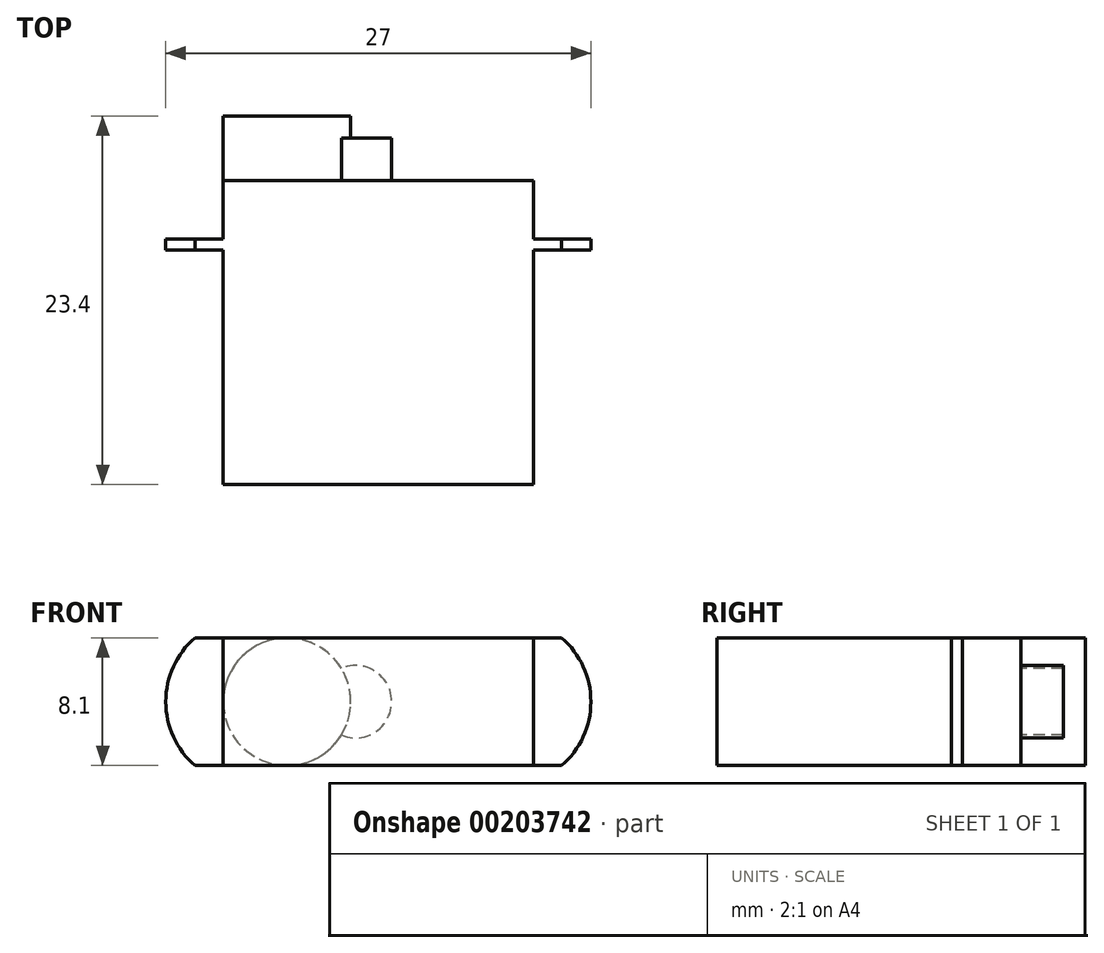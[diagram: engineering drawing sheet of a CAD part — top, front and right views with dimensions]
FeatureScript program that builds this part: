
annotation { "Feature Type Name" : "Feature", "Feature Type Description" : "" }
export const myFeature = defineFeature(function(context is Context, id is Id, definition is map)
    precondition{}
    {
        {
            var Q0;
            Q0=qCreatedBy(makeId("Top.planeOp"),FACE);
            var sketch = newSketch(context, id + "F0", { "sketchPlane" : qUnion([Q0])});
            skLineSegment(sketch, "E0.bottom", {"start": v(9.85, -9.65) * mm, "end": v(-9.85, -9.65) * mm});
            skLineSegment(sketch, "E0.top", {"start": v(9.85, 9.65) * mm, "end": v(-9.85, 9.65) * mm});
            skLineSegment(sketch, "E0.left", {"start": v(9.85, -9.65) * mm, "end": v(9.85, 5.25) * mm});
            skLineSegment(sketch, "E0.right", {"start": v(-9.85, -9.65) * mm, "end": v(-9.85, 5.25) * mm});
            skPoint(sketch, "E0.middle", {"position": v(0, 0) * mm});
            skLineSegment(sketch, "E1.bottom", {"start": v(9.85, 5.95) * mm, "end": v(13.5, 5.95) * mm});
            skLineSegment(sketch, "E1.top", {"start": v(9.85, 5.25) * mm, "end": v(13.5, 5.25) * mm});
            skLineSegment(sketch, "E1.right", {"start": v(13.5, 5.95) * mm, "end": v(13.5, 5.25) * mm});
            skLineSegment(sketch, "E2.trimOffspring", {"start": v(9.85, 5.95) * mm, "end": v(9.85, 9.65) * mm});
            skLineSegment(sketch, "E3.MirrorCS", {"start": v(-13.5, 5.95) * mm, "end": v(-13.5, 5.25) * mm});
            skLineSegment(sketch, "E4.MirrorCS", {"start": v(-9.85, 5.95) * mm, "end": v(-13.5, 5.95) * mm});
            skLineSegment(sketch, "E5.MirrorCS", {"start": v(-9.85, 5.25) * mm, "end": v(-13.5, 5.25) * mm});
            skLineSegment(sketch, "E6.trimOffspring", {"start": v(-9.85, 5.95) * mm, "end": v(-9.85, 9.65) * mm});
            skSolve(sketch);
        }
        {
            var Q0;
            Q0=makeQuery(id+"F0.imprint","IMPRINT",FACE,{"disambiguationData":[TD([[makeQuery(id+"F0.imprint","IMPRINT",EDGE,{"derivedFrom":sQuery(id+"F0.wireOp",EDGE,"E0.bottom")}),-1.0]])]});
            extrude(context, id + "F1", {"entities" : qUnion([Q0]), "depth" : 8.1 * mm, "offsetDistance" : 25 * mm});
        }
        {
            var Q0;
            Q0=makeQuery(id+"F1.opExtrude","SWEPT_FACE",FACE,{"disambiguationData":[OSD([sQuery(id+"F0.wireOp",EDGE,"E1.bottom")])]});
            var sketch = newSketch(context, id + "F2", { "sketchPlane" : qUnion([Q0])});
            skArc(sketch, "E7", {"start": v(-11.65, 8.1) * mm, "mid": v(-13.5, 4.05) * mm, "end": v(-11.65, 0) * mm});
            skArc(sketch, "E8.MirrorCS", {"start": v(11.65, 8.1) * mm, "mid": v(13.5, 4.05) * mm, "end": v(11.65, 0) * mm});
            skLineSegment(sketch, "E9", {"start": v(-11.65, 8.1) * mm, "end": v(-13.5, 8.1) * mm});
            skLineSegment(sketch, "E10", {"start": v(-13.5, 8.1) * mm, "end": v(-13.5, 0) * mm});
            skLineSegment(sketch, "E11", {"start": v(-13.5, 0) * mm, "end": v(-11.65, 0) * mm});
            skLineSegment(sketch, "E12.MirrorCS", {"start": v(11.65, 8.1) * mm, "end": v(13.5, 8.1) * mm});
            skLineSegment(sketch, "E13.MirrorCS", {"start": v(13.5, 8.1) * mm, "end": v(13.5, 0) * mm});
            skLineSegment(sketch, "E14.MirrorCS", {"start": v(13.5, 0) * mm, "end": v(11.65, 0) * mm});
            skSolve(sketch);
        }
        {
            var Q0;
            Q0 = qSketchRegion(id + "F2", true);
            var Q1;
            Q1=makeQuery(id+"F1.opExtrude","SWEPT_FACE",FACE,{"disambiguationData":[OSD([sQuery(id+"F0.wireOp",EDGE,"E1.top")])]});
            extrude(context, id + "F3", {"entities" : qUnion([Q0]), "operationType" : NewBodyOperationType.REMOVE, "endBound" : BoundingType.UP_TO_SURFACE, "oppositeDirection" : true, "depth" : 25 * mm, "endBoundEntityFace" : qUnion([Q1]), "offsetDistance" : 25 * mm});
        }
        {
            var Q0;
            Q0=makeQuery(id+"F1.opExtrude","SWEPT_FACE",FACE,{"disambiguationData":[OSD([sQuery(id+"F0.wireOp",EDGE,"E0.top")])]});
            var sketch = newSketch(context, id + "F4", { "sketchPlane" : qUnion([Q0])});
            skCircle(sketch, "E15", {"center": v(5.8, 4.05) * mm, "radius": 4.05 * mm});
            skArc(sketch, "E16", {"start": v(2.35, 6.17) * mm, "mid": v(-0.85, 4.05) * mm, "end": v(2.35, 1.93) * mm});
            skSolve(sketch);
        }
        {
            var Q0;
            {var subQ0=sQuery(id+"F4.wireOp",EDGE,"E16");var subQ1=sQuery(id+"F4.wireOp",EDGE,"E15");var subQ5=makeQuery(id+"F4.imprint","INTERSECT",VERTEX,{"disambiguationData":[OD(0.0)],"derivedFrom":[subQ1,subQ0]});Q0=makeQuery(id+"F4.imprint","IMPRINT",FACE,{"disambiguationData":[TD([[makeQuery(id+"F4.imprint","IMPRINT",EDGE,{"disambiguationData":[TD([[subQ5,1.0]])],"derivedFrom":subQ1}),1.0]])]});}
            extrude(context, id + "F5", {"entities" : qUnion([Q0]), "operationType" : NewBodyOperationType.ADD, "depth" : 4.1 * mm, "offsetDistance" : 25 * mm});
        }
        {
            var Q0;
            {var subQ0=sQuery(id+"F4.wireOp",EDGE,"E16");Q0=makeQuery(id+"F4.imprint","IMPRINT",FACE,{"disambiguationData":[TD([[makeQuery(id+"F4.imprint","IMPRINT",EDGE,{"derivedFrom":subQ0}),1.0]])]});}
            extrude(context, id + "F6", {"entities" : qUnion([Q0]), "operationType" : NewBodyOperationType.ADD, "depth" : 2.7 * mm, "offsetDistance" : 25 * mm});
        }
    });
